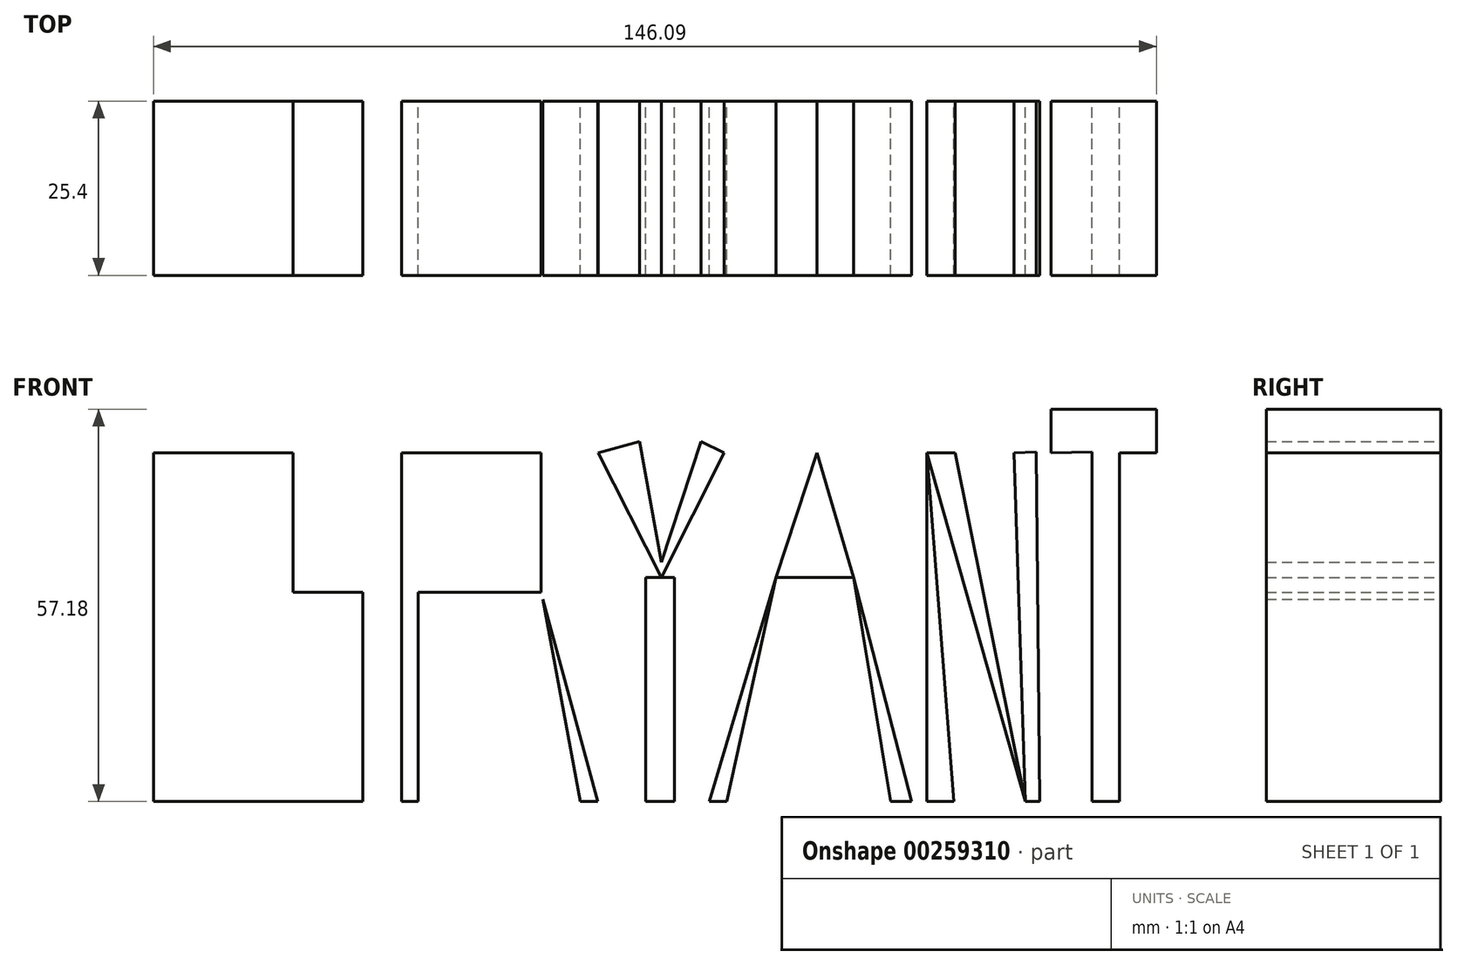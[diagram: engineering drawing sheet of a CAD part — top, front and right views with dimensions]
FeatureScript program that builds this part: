
annotation { "Feature Type Name" : "Feature", "Feature Type Description" : "" }
export const myFeature = defineFeature(function(context is Context, id is Id, definition is map)
    precondition{}
    {
        {
            var Q0;
            Q0=qCreatedBy(makeId("Front.planeOp"),FACE);
            var sketch = newSketch(context, id + "F0", { "sketchPlane" : qUnion([Q0])});
            skLineSegment(sketch, "E0", {"start": v(-73.96, 0) * mm, "end": v(-73.96, 50.8) * mm});
            skLineSegment(sketch, "E1", {"start": v(-73.96, 50.8) * mm, "end": v(-53.64, 50.8) * mm});
            skLineSegment(sketch, "E2", {"start": v(-53.64, 50.8) * mm, "end": v(-53.64, 30.48) * mm});
            skLineSegment(sketch, "E3", {"start": v(-53.64, 30.48) * mm, "end": v(-73.96, 30.48) * mm});
            skLineSegment(sketch, "E4", {"start": v(-53.64, 30.48) * mm, "end": v(-43.48, 30.48) * mm});
            skLineSegment(sketch, "E5", {"start": v(-43.48, 30.48) * mm, "end": v(-43.48, 0) * mm});
            skLineSegment(sketch, "E6", {"start": v(-43.48, 0) * mm, "end": v(-73.96, 0) * mm});
            skLineSegment(sketch, "E7", {"start": v(-37.81, 50.8) * mm, "end": v(-37.81, 0) * mm});
            skLineSegment(sketch, "E8", {"start": v(-37.81, 50.8) * mm, "end": v(-17.5, 50.8) * mm});
            skLineSegment(sketch, "E9", {"start": v(-17.5, 50.8) * mm, "end": v(-17.5, 30.48) * mm});
            skLineSegment(sketch, "E10", {"start": v(-17.5, 30.48) * mm, "end": v(-37.81, 30.48) * mm});
            skLineSegment(sketch, "E11", {"start": v(-17.5, 30.48) * mm, "end": v(-9.24, 0) * mm});
            skLineSegment(sketch, "E12", {"start": v(-37.81, 0) * mm, "end": v(-35.44, 0) * mm});
            skLineSegment(sketch, "E13", {"start": v(-35.44, 0) * mm, "end": v(-35.44, 30.48) * mm});
            skLineSegment(sketch, "E14", {"start": v(-9.24, 0) * mm, "end": v(-11.78, 0) * mm});
            skLineSegment(sketch, "E15", {"start": v(-11.78, 0) * mm, "end": v(-17.23, 29.5) * mm});
            skLineSegment(sketch, "E16", {"start": v(-9.17, 50.8) * mm, "end": v(0, 32.67) * mm});
            skLineSegment(sketch, "E17", {"start": v(0, 32.67) * mm, "end": v(9.15, 50.81) * mm});
            skLineSegment(sketch, "E18", {"start": v(0, 32.67) * mm, "end": v(0, 0) * mm});
            skLineSegment(sketch, "E19", {"start": v(22.7, 50.81) * mm, "end": v(16.73, 32.67) * mm});
            skLineSegment(sketch, "E20", {"start": v(22.7, 50.81) * mm, "end": v(28.02, 32.67) * mm});
            skLineSegment(sketch, "E21", {"start": v(28.02, 32.67) * mm, "end": v(16.73, 32.67) * mm});
            skLineSegment(sketch, "E22", {"start": v(16.73, 32.67) * mm, "end": v(7.03, 0) * mm});
            skLineSegment(sketch, "E23", {"start": v(7.03, 0) * mm, "end": v(9.57, 0) * mm});
            skLineSegment(sketch, "E24", {"start": v(9.57, 0) * mm, "end": v(16.73, 32.67) * mm});
            skLineSegment(sketch, "E25", {"start": v(28.02, 32.67) * mm, "end": v(36.46, 0) * mm});
            skLineSegment(sketch, "E26", {"start": v(36.46, 0) * mm, "end": v(33.44, 0) * mm});
            skLineSegment(sketch, "E27", {"start": v(33.44, 0) * mm, "end": v(28.02, 32.67) * mm});
            skLineSegment(sketch, "E28", {"start": v(38.72, 0) * mm, "end": v(38.72, 50.81) * mm});
            skLineSegment(sketch, "E29", {"start": v(38.72, 50.81) * mm, "end": v(53.02, 0) * mm});
            skLineSegment(sketch, "E30", {"start": v(53.02, 0) * mm, "end": v(51.37, 50.81) * mm});
            skLineSegment(sketch, "E31", {"start": v(38.72, 0) * mm, "end": v(42.64, 0) * mm});
            skLineSegment(sketch, "E32", {"start": v(42.64, 0) * mm, "end": v(38.72, 50.81) * mm});
            skLineSegment(sketch, "E33", {"start": v(38.72, 50.81) * mm, "end": v(42.79, 50.81) * mm});
            skLineSegment(sketch, "E34", {"start": v(42.79, 50.81) * mm, "end": v(53.02, 0) * mm});
            skLineSegment(sketch, "E35", {"start": v(51.37, 50.81) * mm, "end": v(54.63, 50.92) * mm});
            skLineSegment(sketch, "E36", {"start": v(54.63, 50.92) * mm, "end": v(55.15, 0) * mm});
            skLineSegment(sketch, "E37", {"start": v(55.15, 0) * mm, "end": v(53.02, 0) * mm});
            skLineSegment(sketch, "E38", {"start": v(9.15, 50.81) * mm, "end": v(5.81, 52.5) * mm});
            skLineSegment(sketch, "E39", {"start": v(5.81, 52.5) * mm, "end": v(0, 34.86) * mm});
            skLineSegment(sketch, "E40", {"start": v(-9.17, 50.8) * mm, "end": v(-3.15, 52.5) * mm});
            skLineSegment(sketch, "E41", {"start": v(-3.15, 52.5) * mm, "end": v(0, 34.86) * mm});
            skLineSegment(sketch, "E42", {"start": v(0, 32.67) * mm, "end": v(1.94, 32.67) * mm});
            skLineSegment(sketch, "E43", {"start": v(1.94, 32.67) * mm, "end": v(1.94, 0) * mm});
            skLineSegment(sketch, "E44", {"start": v(1.94, 0) * mm, "end": v(0, 0) * mm});
            skLineSegment(sketch, "E45", {"start": v(0, 32.67) * mm, "end": v(-2.24, 32.67) * mm});
            skLineSegment(sketch, "E46", {"start": v(-2.24, 32.67) * mm, "end": v(-2.24, 0) * mm});
            skLineSegment(sketch, "E47", {"start": v(-2.24, 0) * mm, "end": v(0, 0) * mm});
            skLineSegment(sketch, "E48", {"start": v(62.78, 50.92) * mm, "end": v(62.78, 0) * mm});
            skLineSegment(sketch, "E49", {"start": v(62.78, 0) * mm, "end": v(66.77, 0) * mm});
            skLineSegment(sketch, "E50", {"start": v(66.77, 0) * mm, "end": v(66.77, 50.85) * mm});
            skLineSegment(sketch, "E51", {"start": v(62.78, 50.92) * mm, "end": v(66.77, 50.85) * mm});
            skLineSegment(sketch, "E52", {"start": v(66.77, 50.85) * mm, "end": v(72.13, 50.85) * mm});
            skLineSegment(sketch, "E53", {"start": v(72.13, 50.73) * mm, "end": v(72.13, 57.18) * mm});
            skLineSegment(sketch, "E54", {"start": v(72.33, 57.18) * mm, "end": v(56.82, 57.18) * mm});
            skLineSegment(sketch, "E55", {"start": v(56.82, 57.18) * mm, "end": v(56.82, 50.85) * mm});
            skLineSegment(sketch, "E56", {"start": v(56.82, 50.85) * mm, "end": v(62.78, 50.92) * mm});
            skSolve(sketch);
        }
        {
            var Q0;
            Q0 = qSketchRegion(id + "F0", true);
            var Q1;
            Q1=makeQuery(id+"F0.imprint","IMPRINT",FACE,{"disambiguationData":[TD([[makeQuery(id+"F0.imprint","IMPRINT",EDGE,{"derivedFrom":sQuery(id+"F0.wireOp",EDGE,"E51")}),1.0]])]});
            var Q2;
            Q2=makeQuery(id+"F0.imprint","IMPRINT",FACE,{"disambiguationData":[TD([[makeQuery(id+"F0.imprint","IMPRINT",EDGE,{"derivedFrom":sQuery(id+"F0.wireOp",EDGE,"E18")}),-1.0]])]});
            var Q3;
            Q3=makeQuery(id+"F0.imprint","IMPRINT",FACE,{"disambiguationData":[TD([[makeQuery(id+"F0.imprint","IMPRINT",EDGE,{"derivedFrom":sQuery(id+"F0.wireOp",EDGE,"E48")}),1.0]])]});
            var Q4;
            {var subQ0=sQuery(id+"F0.wireOp",EDGE,"E14");Q4=makeQuery(id+"F0.imprint","IMPRINT",FACE,{"disambiguationData":[TD([[makeQuery(id+"F0.imprint","IMPRINT",EDGE,{"derivedFrom":subQ0}),-1.0]])]});}
            var Q5;
            Q5=makeQuery(id+"F0.imprint","IMPRINT",FACE,{"disambiguationData":[TD([[makeQuery(id+"F0.imprint","IMPRINT",EDGE,{"derivedFrom":sQuery(id+"F0.wireOp",EDGE,"E16")}),1.0]])]});
            var Q6;
            Q6=makeQuery(id+"F0.imprint","IMPRINT",FACE,{"disambiguationData":[TD([[makeQuery(id+"F0.imprint","IMPRINT",EDGE,{"derivedFrom":sQuery(id+"F0.wireOp",EDGE,"E19")}),1.0]])]});
            var Q7;
            Q7=makeQuery(id+"F0.imprint","IMPRINT",FACE,{"disambiguationData":[TD([[makeQuery(id+"F0.imprint","IMPRINT",EDGE,{"derivedFrom":sQuery(id+"F0.wireOp",EDGE,"E22")}),1.0]])]});
            var Q8;
            Q8=makeQuery(id+"F0.imprint","IMPRINT",FACE,{"disambiguationData":[TD([[makeQuery(id+"F0.imprint","IMPRINT",EDGE,{"derivedFrom":sQuery(id+"F0.wireOp",EDGE,"E25")}),-1.0]])]});
            var Q9;
            Q9=makeQuery(id+"F0.imprint","IMPRINT",FACE,{"disambiguationData":[TD([[makeQuery(id+"F0.imprint","IMPRINT",EDGE,{"derivedFrom":sQuery(id+"F0.wireOp",EDGE,"E28")}),-1.0]])]});
            var Q10;
            Q10=makeQuery(id+"F0.imprint","IMPRINT",FACE,{"disambiguationData":[TD([[makeQuery(id+"F0.imprint","IMPRINT",EDGE,{"derivedFrom":sQuery(id+"F0.wireOp",EDGE,"E29")}),1.0]])]});
            var Q11;
            Q11=makeQuery(id+"F0.imprint","IMPRINT",FACE,{"disambiguationData":[TD([[makeQuery(id+"F0.imprint","IMPRINT",EDGE,{"derivedFrom":sQuery(id+"F0.wireOp",EDGE,"E30")}),-1.0]])]});
            var Q12;
            {var subQ0=sQuery(id+"F0.wireOp",EDGE,"E3");Q12=makeQuery(id+"F0.imprint","IMPRINT",FACE,{"disambiguationData":[TD([[makeQuery(id+"F0.imprint","IMPRINT",EDGE,{"derivedFrom":subQ0}),1.0]])]});}
            var Q13;
            {var subQ0=sQuery(id+"F0.wireOp",EDGE,"E1");Q13=makeQuery(id+"F0.imprint","IMPRINT",FACE,{"disambiguationData":[TD([[makeQuery(id+"F0.imprint","IMPRINT",EDGE,{"derivedFrom":subQ0}),-1.0]])]});}
            var Q14;
            {var subQ3=sQuery(id+"F0.wireOp",EDGE,"E8");Q14=makeQuery(id+"F0.imprint","IMPRINT",FACE,{"disambiguationData":[TD([[makeQuery(id+"F0.imprint","IMPRINT",EDGE,{"derivedFrom":subQ3}),-1.0]])]});}
            var Q15;
            {var subQ0=sQuery(id+"F0.wireOp",EDGE,"E12");Q15=makeQuery(id+"F0.imprint","IMPRINT",FACE,{"disambiguationData":[TD([[makeQuery(id+"F0.imprint","IMPRINT",EDGE,{"derivedFrom":subQ0}),1.0]])]});}
            var Q16;
            Q16=makeQuery(id+"F0.imprint","IMPRINT",FACE,{"disambiguationData":[TD([[makeQuery(id+"F0.imprint","IMPRINT",EDGE,{"derivedFrom":sQuery(id+"F0.wireOp",EDGE,"E18")}),1.0]])]});
            extrude(context, id + "F1", {"entities" : qUnion([Q0, Q1, Q2, Q3, Q4, Q5, Q6, Q7, Q8, Q9, Q10, Q11, Q12, Q13, Q14, Q15, Q16]), "depth" : 25.4 * mm});
        }
    });
